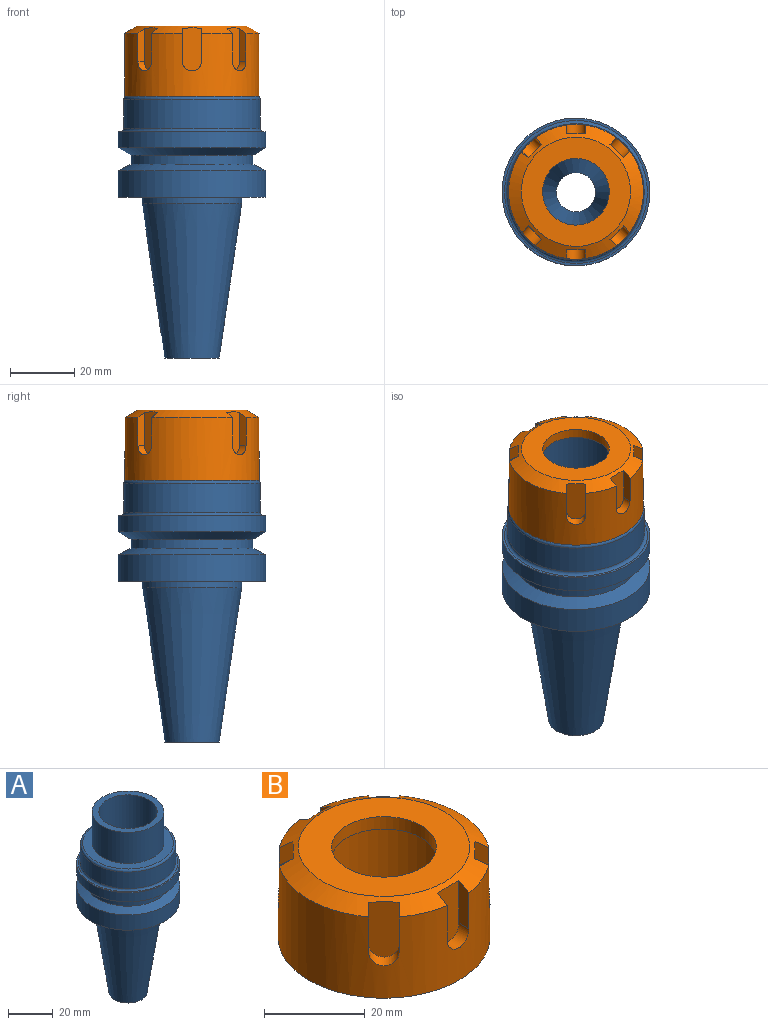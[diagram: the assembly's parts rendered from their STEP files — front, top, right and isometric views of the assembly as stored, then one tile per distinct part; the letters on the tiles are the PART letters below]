
ASSEMBLY  parts=2 mates=1
PART A: 29 faces, bbox 47.7x47.7x98.5 mm
  f0: cylinder r=19mm len=38mm, axis (0,0,-1), area 328.9mm2, adj f12,f25
  f1: cylinder r=13mm len=26mm, axis (0,0,-1), area 1633.6mm2, adj f2,f7
  f2: plane 32x32mm, normal (0,0,1), area 273.3mm2, adj f1,f4
  f3: cylinder r=22.99mm len=45.99mm, axis (0,0,-1), area 722.4mm2, adj f11,f12
  f4: cylinder r=16mm len=32mm, axis (0,0,-1), area 1709mm2, adj f2,f16
  f5: cylinder r=22.99mm len=45.99mm, axis (0,0,-1), area 1202.8mm2, adj f14,f25
  f6: cylinder r=16.25mm len=32.5mm, axis (0,0,-1), area 1123.1mm2, adj f7,f26
  f7: plane 32.5x32.5mm, normal (0,0,-1), area 298.6mm2, adj f1,f6
  f8: cylinder r=6.12mm len=12.24mm, axis (0,0,-1), area 133.4mm2, adj f9,f13
  f9: torus R=7.12mm, axis (0,0,1), area 64mm2, adj f8,f10
  f10: plane 17x17mm, normal (0,0,-1), area 67.7mm2, adj f9,f18
  f11: plane 45.99x45.99mm, normal (0,0,1), area 105.8mm2, adj f3,f27
  f12: cone r=19mm half-angle=58.8deg, axis (0,0,1), area 616.2mm2, adj f0,f3
  f13: cone r=5.47mm half-angle=8.3deg, axis (0,0,1), area 2976.4mm2, adj f8,f22
  f14: plane 45.99x45.99mm, normal (0,0,-1), area 906.3mm2, adj f5,f17
  f15: cylinder r=21.25mm len=42.5mm, axis (0,0,-1), area 1201.7mm2, adj f27,f28
  f16: plane 40.5x40.5mm, normal (0,0,1), area 484mm2, adj f4,f28
  f17: cylinder r=15.5mm len=31mm, axis (0,0,-1), area 194.8mm2, adj f14,f18
  f18: cone r=8.5mm half-angle=8.3deg, axis (0,0,1), area 3657.4mm2, adj f10,f17
  f19: cone r=16mm half-angle=58.8deg, axis (0,0,1), area 528.2mm2, adj f20,f24
  f20: cylinder r=19.99mm len=39.99mm, axis (0,0,-1), area 39mm2, adj f19,f26
  f21: cylinder r=19.99mm len=39.99mm, axis (0,0,-1), area 436.2mm2, adj f22,f23
  f22: plane 39.99x39.99mm, normal (0,0,1), area 708.8mm2, adj f13,f21
  f23: cone r=16mm half-angle=63.4deg, axis (0,0,-1), area 505.1mm2, adj f21,f24
  f24: cylinder r=16mm len=32mm, axis (0,0,-1), area 633.2mm2, adj f19,f23
  f25: cone r=19mm half-angle=63.4deg, axis (0,0,-1), area 589.3mm2, adj f0,f5
  f26: plane 39.99x39.99mm, normal (0,0,-1), area 426.4mm2, adj f6,f20
  f27: torus R=22.25mm, axis (0,0,1), area 213.3mm2, adj f11,f15
  f28: torus R=20.25mm, axis (0,0,1), area 206.1mm2, adj f15,f16
PART B: 32 faces, bbox 42.6x42.6x22.4 mm
  f0: cylinder r=3mm len=6.36mm, axis (-0.71,-0.71,0), area 27.3mm2, adj f2,f17,f18,f19
  f1: cylinder r=3mm len=6.36mm, axis (0.71,-0.71,0), area 27.3mm2, adj f2,f23,f24,f25
  f2: cylinder r=21mm len=42mm, axis (0,0,1), area 2182mm2, adj f0,f1,f3,f4,f5,f6,f8,f9
  f3: cylinder r=3mm len=6.36mm, axis (-0.71,-0.71,0), area 27.3mm2, adj f2,f8,f9,f10
  f4: cylinder r=3mm len=6mm, axis (0,-1,0), area 27.3mm2, adj f2,f11,f12,f13
  f5: cylinder r=3mm len=6.36mm, axis (0.71,-0.71,0), area 27.3mm2, adj f2,f14,f15,f16
  f6: cylinder r=3mm len=6mm, axis (0,1,0), area 27.3mm2, adj f2,f20,f21,f22
  f7: plane 34x34mm, normal (0,0,1), area 569.8mm2, adj f26,f29
  f8: plane 10.33x2.02mm, normal (-0.71,0.71,0), area 26.4mm2, adj f2,f3,f10,f26
  f9: plane 10.33x2.02mm, normal (0.71,-0.71,0), area 26.4mm2, adj f2,f3,f10,f26
  f10: plane 14x4.82mm, normal (0.71,0.71,0), area 76.4mm2, adj f3,f8,f9,f26
  f11: plane 10.33x2.83mm, normal (-1,0,0), area 26.4mm2, adj f2,f4,f13,f26
  f12: plane 10.33x2.83mm, normal (1,0,0), area 26.4mm2, adj f2,f4,f13,f26
  f13: plane 14x6.57mm, normal (0,1,0), area 76.4mm2, adj f4,f11,f12,f26
  f14: plane 10.33x2.02mm, normal (0.71,0.71,0), area 26.4mm2, adj f2,f5,f16,f27
  f15: plane 10.33x2.02mm, normal (-0.71,-0.71,0), area 26.4mm2, adj f2,f5,f16,f26
  f16: plane 14x4.82mm, normal (-0.71,0.71,0), area 76.4mm2, adj f5,f14,f15,f26
  f17: plane 10.33x2.02mm, normal (-0.71,0.71,0), area 26.4mm2, adj f0,f2,f19,f26
  f18: plane 10.33x2.02mm, normal (0.71,-0.71,0), area 26.4mm2, adj f0,f2,f19,f26
  f19: plane 14x4.82mm, normal (-0.71,-0.71,0), area 76.4mm2, adj f0,f17,f18,f26
  f20: plane 10.33x2.83mm, normal (-1,0,0), area 26.4mm2, adj f2,f6,f22,f26
  f21: plane 10.33x2.83mm, normal (1,0,0), area 26.4mm2, adj f2,f6,f22,f26
  f22: plane 14x6.57mm, normal (0,-1,0), area 76.4mm2, adj f6,f20,f21,f26
  f23: plane 10.33x2.02mm, normal (0.71,0.71,0), area 26.4mm2, adj f1,f2,f25,f26
  f24: plane 10.33x2.02mm, normal (-0.71,-0.71,0), area 26.4mm2, adj f1,f2,f25,f26
  f25: plane 14x4.82mm, normal (0.71,-0.71,0), area 76.4mm2, adj f1,f23,f24,f26
  f26: cone r=1.73mm half-angle=60deg, axis (0,0,-1), area 435.5mm2, adj f2,f7,f8,f9,f10,f11,f12,f13
  f27: cone r=1.73mm half-angle=60deg, axis (0,0,-1), area 0.7mm2, adj f2,f14,f26
  f28: cylinder r=16.15mm len=32.3mm, axis (0,0,1), area 1914.8mm2, adj f30,f31
  f29: cylinder r=10.38mm len=20.75mm, axis (0,0,1), area 195.6mm2, adj f7,f30
  f30: plane 32.3x32.3mm, normal (0,0,-1), area 481.2mm2, adj f28,f29
  f31: plane 42x42mm, normal (0,0,-1), area 566mm2, adj f2,f28
PLACE A t=(-29.45,-13.01,3.5)mm fixed
PLACE B t=(-29.45,-13.01,3.37)mm
MATE fastened B.f2 <-> A.f0  axis (0,0,1) through (-29.45,-13.01,35.75)mm
